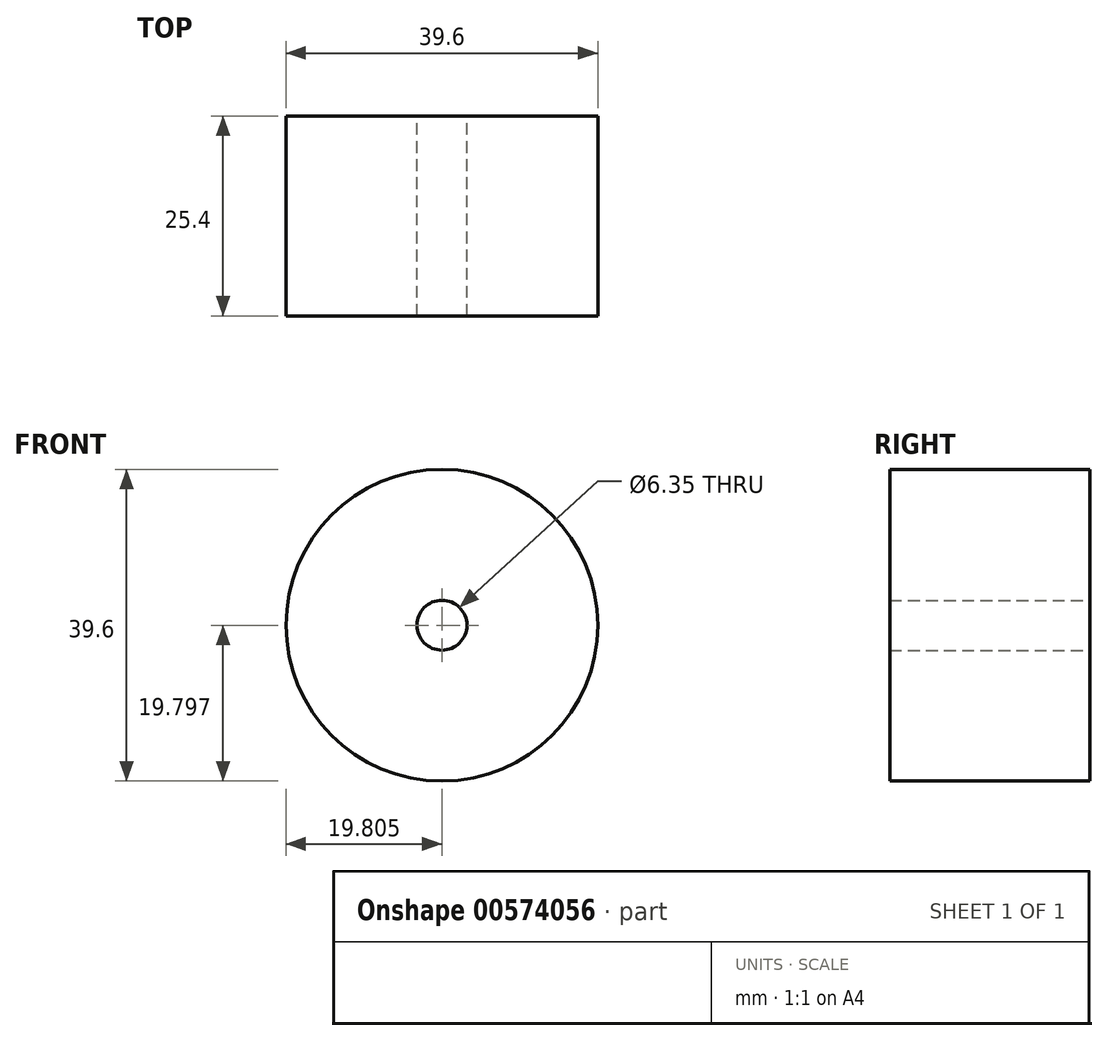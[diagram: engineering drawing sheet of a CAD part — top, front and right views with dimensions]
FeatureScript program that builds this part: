
annotation { "Feature Type Name" : "Feature", "Feature Type Description" : "" }
export const myFeature = defineFeature(function(context is Context, id is Id, definition is map)
    precondition{}
    {
        {
            var Q0;
            Q0=qCreatedBy(makeId("Front.planeOp"),FACE);
            var sketch = newSketch(context, id + "F0", { "sketchPlane" : qUnion([Q0])});
            skCircle(sketch, "E0", {"center": v(-23.68, 12.63) * mm, "radius": 19.8 * mm});
            skSolve(sketch);
        }
        {
            var Q0;
            Q0=makeQuery(id+"F0.imprint","IMPRINT",FACE,{"disambiguationData":[TD([[makeQuery(id+"F0.imprint","IMPRINT",EDGE,{"derivedFrom":sQuery(id+"F0.wireOp",EDGE,"E0")}),1.0]])]});
            extrude(context, id + "F1", {"entities" : qUnion([Q0]), "depth" : 25.4 * mm, "offsetDistance" : 25.4 * mm});
        }
        {
            var Q0;
            Q0=sQuery(id+"F0.wireOp",VERTEX,"E0.center");
            var Q1;
            Q1=makeQuery(id+"F1.opExtrude","SWEPT_BODY",BODY,{"disambiguationData":[OSD([sQuery(id+"F0.wireOp",EDGE,"E0")])]});
            hole(context, id + "F2", {"style" : HoleStyle.SIMPLE, "endStyle" : HoleEndStyle.THROUGH, "oppositeDirection" : true, "holeDiameter" : 6.35 * mm, "majorDiameter" : 6.35 * mm, "isTappedThrough" : true, "tappedDepth" : 12.7 * mm, "tapClearance" : 3, "locations" : qUnion([Q0]), "scope" : qUnion([Q1])});
        }
    });
